# Revit family: Electronics_Community-Point-Source_Biamp_Loudspeaker_R_1
name_source: partatom
category: Communication Devices
units: mm (PartAtom-declared; Revit-internal decimal feet)

## family parameters
Cut with Voids When Loaded = No
Host = Face
Maintain Annotation Orientation = No
OmniClass Number = 23.85.10.11.14.14.14
OmniClass Title = Loudspeakers
Part Type = Normal
Room Calculation Point = No
Round Connector Dimension = Use Diameter
Shared = No

## types (3) — shared parameters
Connector Description = Terminal strip; 200W continuous, 500W program 40 volts RMS, 89 volts momentary peak
Crossover Frequency = 1.2 kHz
Default Elevation = 48 "
Depth = 29.76 "
Description = R1 Two-Way Horn Loaded Weather-Resistant Full-Range Loudspeaker
Driver Protection = PowerSense™ DDP
Drivers = LF 1 x 12” weather-treated, Ferrofluid-cooled HF 1 x 1” exit, titanium diaphragm
Enclosure = Hand-laminated fiberglass, light grey gelcoat
Environmental Performance = IEC529 IP55W rating with a minimum 5-degree downward aiming angle
Grill Material = Biamp - Plastic - Gray(Grid)
Grille = 3-layer WeatherStop™, light grey (Zinc-rich epoxy dual-layer powder coated perforated steel grille, foam, woven poly mesh)
Height = 24.76 "
Housing Material = Biamp - Plastic - Gray
Input Connection = 12 foot (4 m) SJOW #16 gauge
Loudspeaker Type = 2-way horn loaded coaxial, weather-resistant
Manufacturer = Biamp
Max Input Ratings = 200W continuous, 500W program 40 volts RMS, 89 volts momentary peak
Max value position = 3
Mounting/Rigging Provisions = (5) 1/2-13 rigging points
Nominal Impedance = 8 ohms
Operating Range = 90 Hz to 16 kHz 110 Hz to 10 kHz (±4 dB)
Product Documentation Link = https://downloads.biamp.com
Product Page URL = https://www.biamp.com
Product data url = https://www.bimobject.com
Recommended Power Amplifier = 420W to 600W @ 8 ohms
Recommended Signal = 90 Hz high pass filter
Required Accessories = 90 Hz high pass filter
URL = https://www.biamp.com
Weight = 55.56 lb
Width = 24.76 "
Yoke Material = Biamp - Metal - Gray

## per-type parameters (varying)
| type | Axial Q / DI | Maximum Output | Minimum Impedance | Nominal –6dB | Sensitivity (1W/1m) |
| R1-64Z | 31.5 / 15, 1 kHz to 16 kHz | 128 dB SPL / 135 dB SPL (peak) | 5.5 ohms @ 230 Hz | 50° H (+4° / -19°, 1 kHz to 16 kHz) 35° V (+7° / -5°, 1 kHz to 16 kHz) 100° H x 100° V (400 Hz) | 105 dB SPL (100 Hz to 16 kHz 1/3 octave bands) 106 dB SPL (250 Hz to 4 kHz speech range) |
| R1-66Z | 20.3 / 13.1, 1 kHz to 16 kHz | 128 dB SPL / 135 dB SPL (peak) | 5.7 ohms @ 230 Hz | 60° H (+18° / -20°, 1 kHz to 16 kHz) 60° V (+13° / -16°, 1 kHz to 16 kHz) 100° H x 100° V (400 Hz) | 105 dB SPL (100 Hz to 16 kHz 1/3 octave bands) 106 dB SPL (250 Hz to 4 kHz speech range) |
| R1-94Z | 29.7 / 14.7, 1 kHz to 16 kHz | 127 dB SPL / 134 dB SPL (peak) | 5.7 ohms @ 230 Hz | 80° H (+0° / -49°, 1 kHz to 16 kHz) 35° V (+4° / -10°, 1 kHz to 16 kHz) 100° H x 100° V (400 Hz) | 104 dB SPL (100 Hz to 16 kHz 1/3 octave bands) 105 dB SPL (250 Hz to 4 kHz speech range) |

note: column(s) folded — value = type name in every type: Model

## geometry (parser evidence)
native form markers: Sweep x4
no freeform markers — native parametric forms only
